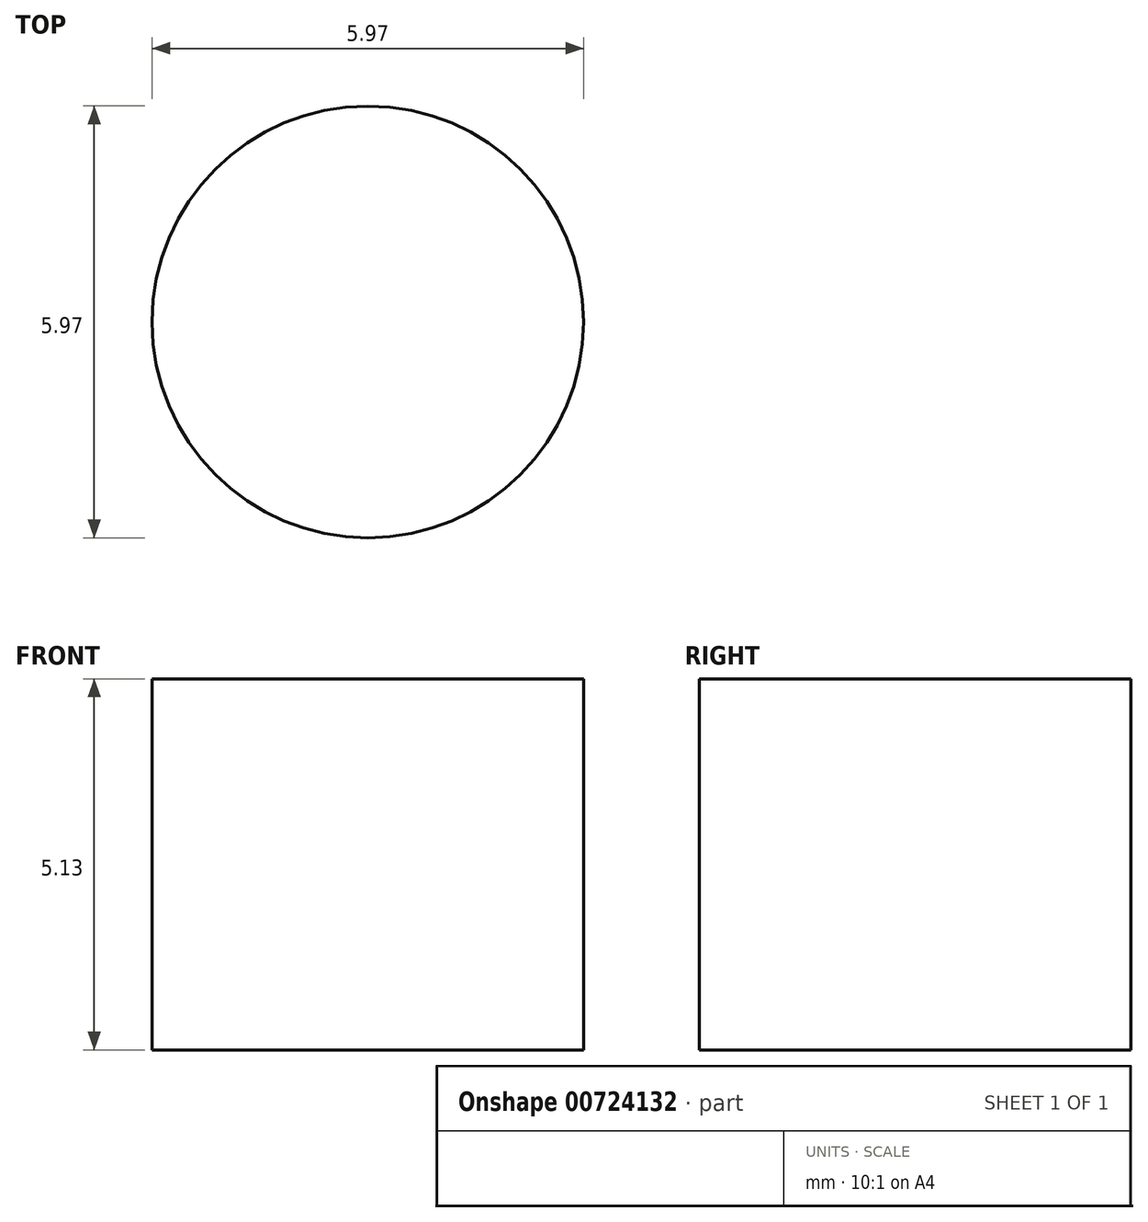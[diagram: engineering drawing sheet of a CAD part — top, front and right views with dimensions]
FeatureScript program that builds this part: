
annotation { "Feature Type Name" : "Feature", "Feature Type Description" : "" }
export const myFeature = defineFeature(function(context is Context, id is Id, definition is map)
    precondition{}
    {
        {
            var Q0;
            Q0=qCreatedBy(makeId("Top.planeOp"),FACE);
            var sketch = newSketch(context, id + "F0", { "sketchPlane" : qUnion([Q0])});
            skCircle(sketch, "E0", {"center": v(-117.47, -26.2) * mm, "radius": 2.98 * mm});
            skSolve(sketch);
        }
        {
            var Q0;
            Q0=makeQuery(id+"F0.imprint","IMPRINT",FACE,{"disambiguationData":[TD([[makeQuery(id+"F0.imprint","IMPRINT",EDGE,{"derivedFrom":sQuery(id+"F0.wireOp",EDGE,"E0")}),1.0]])]});
            extrude(context, id + "F1", {"entities" : qUnion([Q0]), "depth" : 5.13 * mm, "offsetDistance" : 25.4 * mm});
        }
    });
